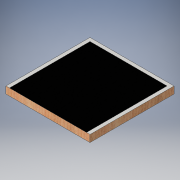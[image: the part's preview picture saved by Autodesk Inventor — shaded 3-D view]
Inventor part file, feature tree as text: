
AUTODESK INVENTOR PART (.ipt)
format: ipt  version: 2016 (Build 200138000, 138)  size: 116,736 bytes
history: native  units: in
note: dims shown in document units (in); Inventor stores cm internally (conversion verified against a paired STEP export)
features: extrude x2, sketch x2
ambient origin geometry x8: Origin, YZ Plane, XZ Plane, XY Plane, X Axis, Y Axis, Z Axis, Center Point
bodies: Solid1 (feature_tree)
feature tree (4):
  extrude  "Extrusion1"  Depth=12.0in
  extrude  "Extrusion2"  Depth=11.0in
  sketch  "Sketch1"  dims[d0=12.0in d1=12.0in]
  sketch  "Sketch2"  dims[d2=11.0in d3=11.0in d4=1.0in d5=0.0in d6=12.0in d7=11.0in d8=11.0in d9=0.0001in d10=0.0in]
